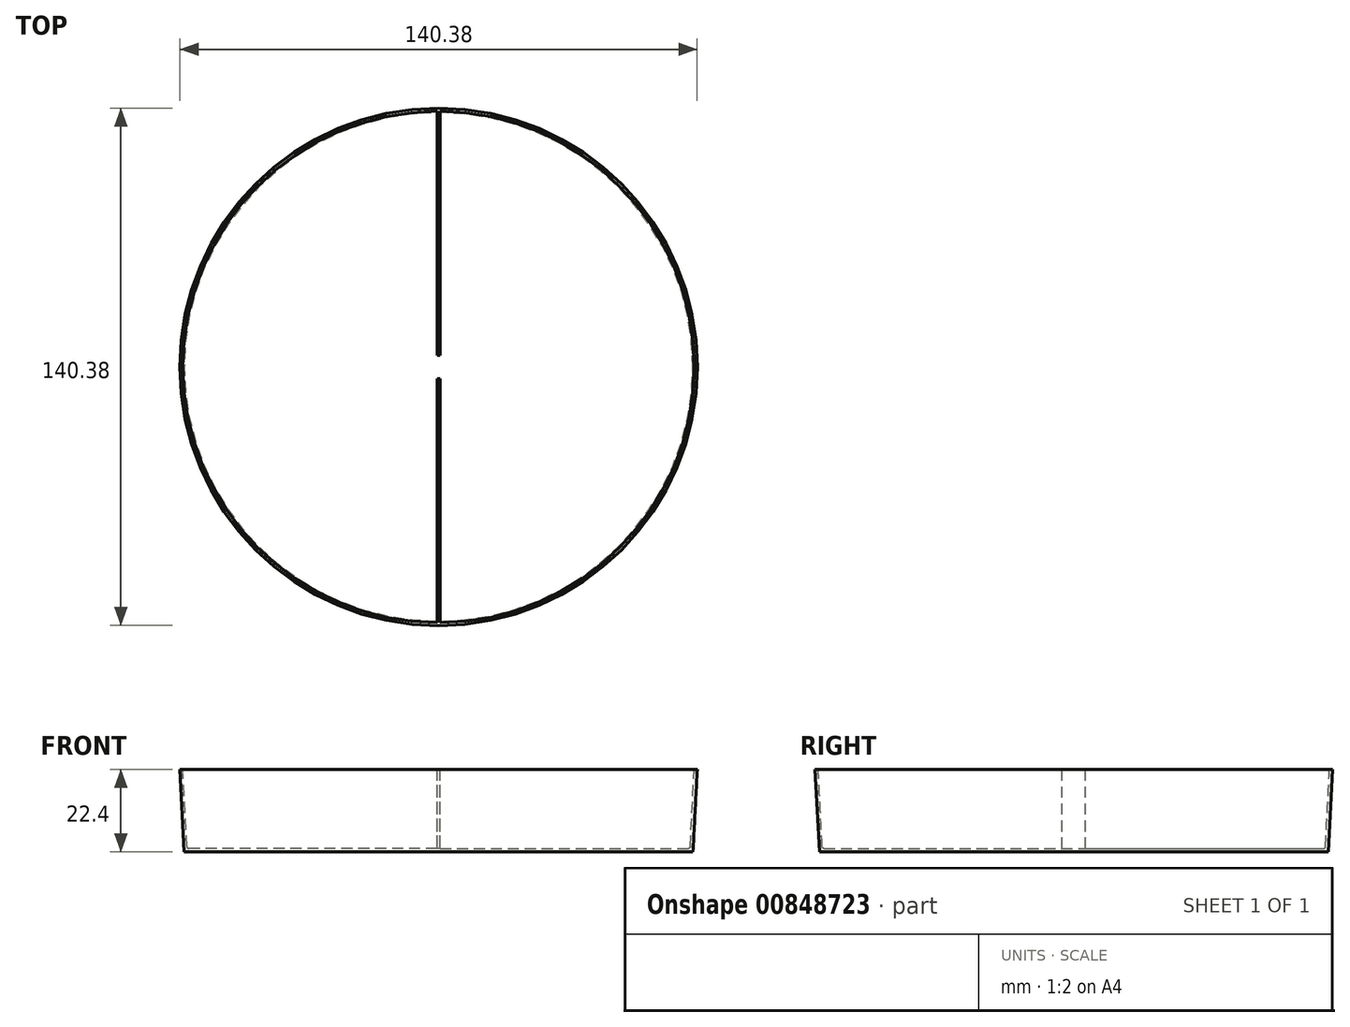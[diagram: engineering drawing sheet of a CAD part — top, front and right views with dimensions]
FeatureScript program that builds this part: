
annotation { "Feature Type Name" : "Feature", "Feature Type Description" : "" }
export const myFeature = defineFeature(function(context is Context, id is Id, definition is map)
    precondition{}
    {
        {
            var Q0;
            Q0=qCreatedBy(makeId("Top.planeOp"),FACE);
            var sketch = newSketch(context, id + "F0", { "sketchPlane" : qUnion([Q0])});
            skCircle(sketch, "E0", {"center": v(0, 0) * mm, "radius": 69.02 * mm});
            skSolve(sketch);
        }
        {
            var Q0;
            Q0=makeQuery(id+"F0.imprint","IMPRINT",FACE,{"disambiguationData":[TD([[makeQuery(id+"F0.imprint","IMPRINT",EDGE,{"derivedFrom":sQuery(id+"F0.wireOp",EDGE,"E0")}),1.0]])]});
            extrude(context, id + "F1", {"entities" : qUnion([Q0]), "depth" : .9 * mm, "offsetDistance" : 25.4 * mm});
        }
        {
            var Q0;
            Q0=qCreatedBy(makeId("Front.planeOp"),FACE);
            var sketch = newSketch(context, id + "F2", { "sketchPlane" : qUnion([Q0])});
            skLineSegment(sketch, "E1", {"start": v(0, 0) * mm, "end": v(0, 22.4) * mm});
            skLineSegment(sketch, "E2", {"start": v(-69.02, 0) * mm, "end": v(-69.02, 0.9) * mm});
            skLineSegment(sketch, "E3", {"start": v(-69.02, 0) * mm, "end": v(-70.2, 22.4) * mm});
            skLineSegment(sketch, "E4", {"start": v(-70.2, 22.4) * mm, "end": v(-69.4, 22.4) * mm});
            skLineSegment(sketch, "E5", {"start": v(-69.4, 22.4) * mm, "end": v(-68.22, 0) * mm});
            skLineSegment(sketch, "E6", {"start": v(-69.02, 0) * mm, "end": v(-68.22, 0) * mm});
            skSolve(sketch);
        }
        {
            var Q0;
            Q0 = qSketchRegion(id + "F2", true);
            var Q1;
            Q1=sQuery(id+"F2.wireOp",EDGE,"E1");
            revolve(context, id + "F3", {"operationType" : NewBodyOperationType.ADD, "surfaceOperationType" : NewSurfaceOperationType.NEW, "entities" : qUnion([Q0]), "axis" : qUnion([Q1]), "revolveType" : RevolveType.FULL});
        }
        {
            var Q0;
            Q0=makeQuery(id+"F3.boolean.opBoolean","INTERSECT",EDGE,{"derivedFrom":[makeQuery(id+"F1.opExtrude","CAP_FACE",FACE,{"disambiguationData":[OSD([sQuery(id+"F0.wireOp",EDGE,"E0")])],"isStart":false}),makeQuery(id+"F3.opRevolve","SWEPT_FACE",FACE,{"disambiguationData":[OSD([sQuery(id+"F2.wireOp",EDGE,"E5")])]})]});
            fillet(context, id + "F4", {"entities" : qUnion([Q0]), "radius" : 0.5 * mm, "tangentPropagation" : true, "allowEdgeOverflow" : false});
        }
        {
            var Q0;
            Q0=qCreatedBy(makeId("Front.planeOp"),FACE);
            var sketch = newSketch(context, id + "F5", { "sketchPlane" : qUnion([Q0])});
            skLineSegment(sketch, "E7.0", {"start": v(70.2, 22.4) * mm, "end": v(-70.2, 22.4) * mm});
            skLineSegment(sketch, "E8.0", {"start": v(-69.02, 0) * mm, "end": v(69.02, 0) * mm});
            skLineSegment(sketch, "E9.bottom", {"start": v(-0.4, 22.4) * mm, "end": v(0.4, 22.4) * mm});
            skLineSegment(sketch, "E9.top", {"start": v(-0.4, 0) * mm, "end": v(0.4, 0) * mm});
            skLineSegment(sketch, "E9.left", {"start": v(-0.4, 22.4) * mm, "end": v(-0.4, 0) * mm});
            skLineSegment(sketch, "E9.right", {"start": v(0.4, 22.4) * mm, "end": v(0.4, 0) * mm});
            skSolve(sketch);
        }
        {
            var Q0;
            {var subQ0=sQuery(id+"F5.wireOp",EDGE,"E9.left");Q0=makeQuery(id+"F5.imprint","IMPRINT",FACE,{"disambiguationData":[TD([[makeQuery(id+"F5.imprint","IMPRINT",EDGE,{"derivedFrom":subQ0}),1.0]])]});}
            var Q1;
            Q1=makeQuery(id+"F3.opRevolve","SWEPT_FACE",FACE,{"disambiguationData":[OSD([sQuery(id+"F2.wireOp",EDGE,"E5")])]});
            extrude(context, id + "F6", {"entities" : qUnion([Q0]), "operationType" : NewBodyOperationType.ADD, "endBound" : BoundingType.UP_TO_SURFACE, "depth" : 25.4 * mm, "endBoundEntityFace" : qUnion([Q1]), "offsetDistance" : 25.4 * mm});
        }
        {
            var Q0;
            Q0=makeQuery(id+"F6.opExtrude","CAP_FACE",FACE,{"disambiguationData":[OSD([sQuery(id+"F5.wireOp",EDGE,"E7.0"),sQuery(id+"F5.wireOp",EDGE,"E8.0"),sQuery(id+"F5.wireOp",EDGE,"E9.left"),sQuery(id+"F5.wireOp",EDGE,"E9.right")])],"isStart":true});
            var sketch = newSketch(context, id + "F7", { "sketchPlane" : qUnion([Q0])});
            skLineSegment(sketch, "E10.0.0", {"start": v(-0.4, 0.9) * mm, "end": v(0.4, 0.9) * mm});
            skLineSegment(sketch, "E10.0.1", {"start": v(0.4, 0.9) * mm, "end": v(0.4, 22.4) * mm});
            skLineSegment(sketch, "E10.0.2", {"start": v(0.4, 22.4) * mm, "end": v(-0.4, 22.4) * mm});
            skLineSegment(sketch, "E10.0.3", {"start": v(-0.4, 22.4) * mm, "end": v(-0.4, 0.9) * mm});
            skSolve(sketch);
        }
        {
            var Q0;
            Q0=makeQuery(id+"F7.imprint","IMPRINT",FACE,{"disambiguationData":[TD([[makeQuery(id+"F7.imprint","IMPRINT",EDGE,{"derivedFrom":sQuery(id+"F7.wireOp",EDGE,"E10.0.0")}),-1.0]])]});
            var Q1;
            Q1=makeQuery(id+"F3.opRevolve","SWEPT_FACE",FACE,{"disambiguationData":[OSD([sQuery(id+"F2.wireOp",EDGE,"E5")])]});
            extrude(context, id + "F8", {"entities" : qUnion([Q0]), "operationType" : NewBodyOperationType.ADD, "endBound" : BoundingType.UP_TO_SURFACE, "depth" : 25.4 * mm, "endBoundEntityFace" : qUnion([Q1]), "offsetDistance" : 25.4 * mm});
        }
        {
            var Q0;
            Q0=makeQuery(id+"F8.boolean.opBoolean","MERGE",FACE,{"derivedFrom":[makeQuery(id+"F6.boolean.opBoolean","MERGE",FACE,{"derivedFrom":[makeQuery(id+"F3.opRevolve","SWEPT_FACE",FACE,{"disambiguationData":[OSD([sQuery(id+"F2.wireOp",EDGE,"E4")])]}),makeQuery(id+"F6.opExtrude","SWEPT_FACE",FACE,{"disambiguationData":[OSD([sQuery(id+"F5.wireOp",EDGE,"E7.0")])]})]}),makeQuery(id+"F8.opExtrude","SWEPT_FACE",FACE,{"disambiguationData":[OSD([sQuery(id+"F7.wireOp",EDGE,"E10.0.2")])]})]});
            var sketch = newSketch(context, id + "F9", { "sketchPlane" : qUnion([Q0])});
            skLineSegment(sketch, "E11.bottom", {"start": v(-3.08, 3.18) * mm, "end": v(4.5, 3.18) * mm});
            skLineSegment(sketch, "E11.top", {"start": v(-3.08, -3.18) * mm, "end": v(4.5, -3.18) * mm});
            skLineSegment(sketch, "E11.left", {"start": v(-3.08, 3.18) * mm, "end": v(-3.08, -3.18) * mm});
            skLineSegment(sketch, "E11.right", {"start": v(4.5, 3.18) * mm, "end": v(4.5, -3.18) * mm});
            skSolve(sketch);
        }
        {
            var Q0;
            {var subQ0=sQuery(id+"F9.wireOp",EDGE,"E11.bottom");var subQ1=sQuery(id+"F7.wireOp",EDGE,"E10.0.2");var subQ2=sQuery(id+"F5.wireOp",EDGE,"E7.0");var subQ3=makeQuery(id+"F8.boolean.opBoolean","MERGE",EDGE,{"derivedFrom":[makeQuery(id+"F6.opExtrude","SWEPT_EDGE",EDGE,{"disambiguationData":[OSD([subQ2,sQuery(id+"F5.wireOp",EDGE,"E9.left")])]}),makeQuery(id+"F8.opExtrude","SWEPT_EDGE",EDGE,{"disambiguationData":[OSD([sQuery(id+"F7.wireOp",EDGE,"E10.0.1"),subQ1])]})]});var subQ4=makeQuery(id+"F9.imprint","INTERSECT",VERTEX,{"derivedFrom":[subQ3,subQ0]});Q0=makeQuery(id+"F9.imprint","IMPRINT",FACE,{"disambiguationData":[TD([[makeQuery(id+"F9.imprint","IMPRINT",EDGE,{"disambiguationData":[TD([[subQ4,-1.0]])],"derivedFrom":subQ0}),-1.0]])]});}
            var Q1;
            {var subQ0=sQuery(id+"F0.wireOp",EDGE,"E0");Q1=makeQuery(id+"F8.boolean.opBoolean","SPLIT",FACE,{"disambiguationData":[TD([makeQuery(id+"F6.opExtrude","SWEPT_FACE",FACE,{"disambiguationData":[OSD([sQuery(id+"F5.wireOp",EDGE,"E9.right")])]})])],"derivedFrom":makeQuery(id+"F1.opExtrude","CAP_FACE",FACE,{"disambiguationData":[OSD([subQ0])],"isStart":false})});}
            extrude(context, id + "F10", {"entities" : qUnion([Q0]), "operationType" : NewBodyOperationType.REMOVE, "endBound" : BoundingType.UP_TO_SURFACE, "oppositeDirection" : true, "depth" : 25.4 * mm, "endBoundEntityFace" : qUnion([Q1]), "offsetDistance" : 25.4 * mm});
        }
    });
